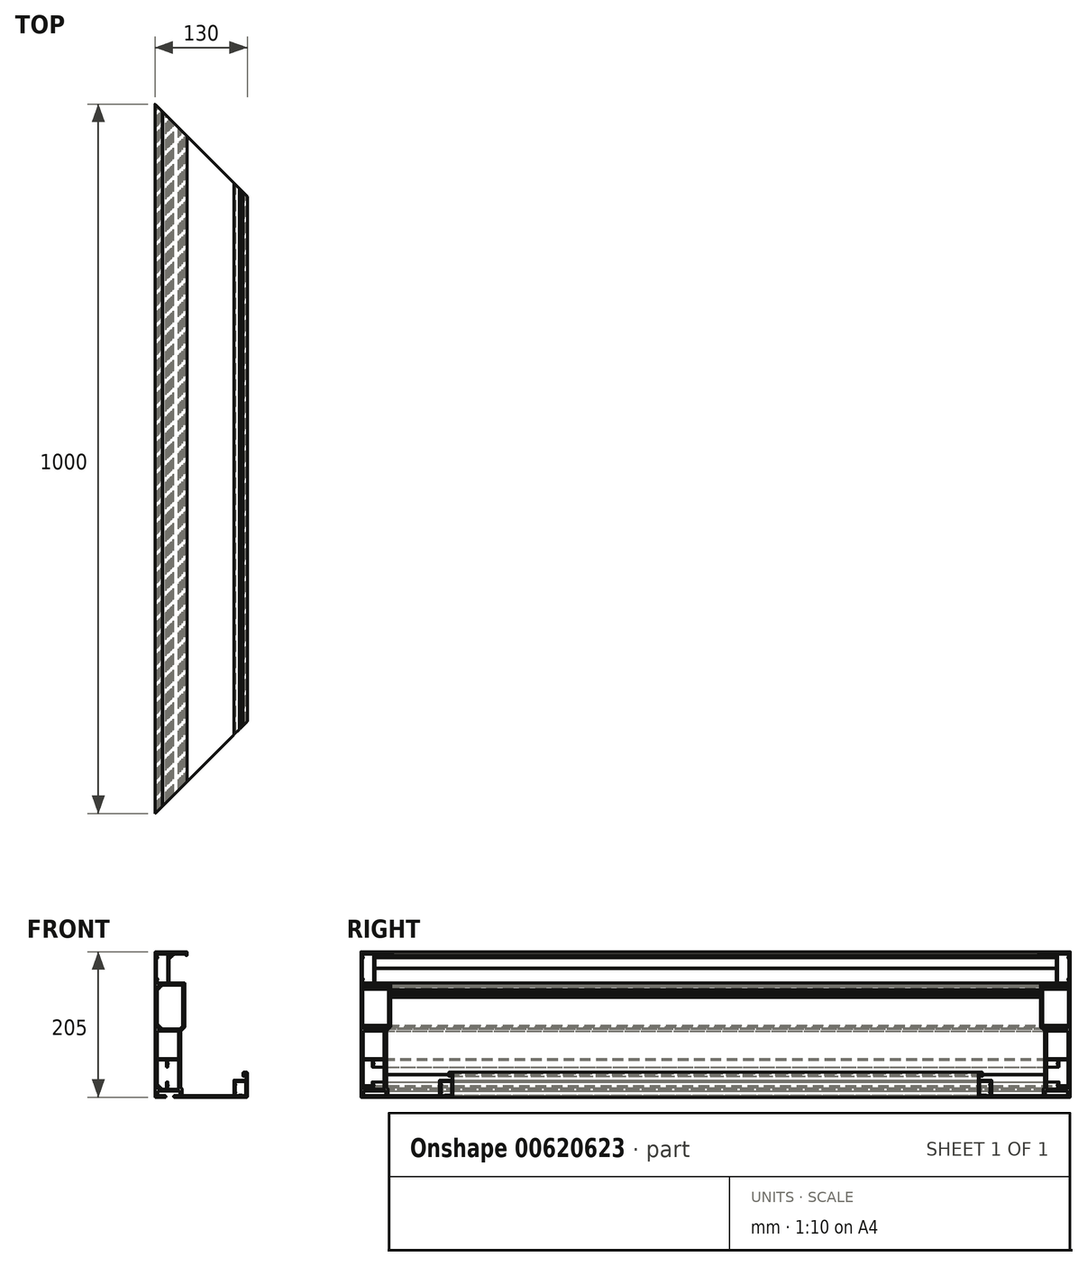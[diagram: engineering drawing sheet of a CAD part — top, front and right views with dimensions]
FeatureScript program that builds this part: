
annotation { "Feature Type Name" : "Feature", "Feature Type Description" : "" }
export const myFeature = defineFeature(function(context is Context, id is Id, definition is map)
    precondition{}
    {
        {
            var Q0;
            Q0=qCreatedBy(makeId("Front.planeOp"),FACE);
            var sketch = newSketch(context, id + "F0", { "sketchPlane" : qUnion([Q0])});
            skArc(sketch, "E0", {"start": v(124.96, 29.38) * mm, "mid": v(124.97, 29.38) * mm, "end": v(124.98, 29.38) * mm});
            skLineSegment(sketch, "E1", {"start": v(10.55, 204.65) * mm, "end": v(10.2, 205) * mm});
            skLineSegment(sketch, "E2", {"start": v(10.2, 205) * mm, "end": v(0.5, 205) * mm});
            skArc(sketch, "E3", {"start": v(0.5, 205) * mm, "mid": v(0.15, 204.85) * mm, "end": v(0, 204.5) * mm});
            skLineSegment(sketch, "E4", {"start": v(0, 204.5) * mm, "end": v(0, 0.5) * mm});
            skArc(sketch, "E5", {"start": v(0, 0.5) * mm, "mid": v(0.15, 0.15) * mm, "end": v(0.5, 0) * mm});
            skLineSegment(sketch, "E6", {"start": v(0.5, 0) * mm, "end": v(14.86, 0) * mm});
            skArc(sketch, "E7", {"start": v(14.86, 0) * mm, "mid": v(15, 0.06) * mm, "end": v(15.06, 0.2) * mm});
            skLineSegment(sketch, "E8", {"start": v(15.06, 0.2) * mm, "end": v(15.06, 1.8) * mm});
            skArc(sketch, "E9", {"start": v(15.06, 1.8) * mm, "mid": v(15, 1.94) * mm, "end": v(14.86, 2) * mm});
            skLineSegment(sketch, "E10", {"start": v(14.86, 2) * mm, "end": v(4.18, 2) * mm});
            skArc(sketch, "E11", {"start": v(4.18, 2) * mm, "mid": v(4.04, 2.06) * mm, "end": v(3.98, 2.2) * mm});
            skLineSegment(sketch, "E12", {"start": v(3.98, 2.2) * mm, "end": v(3.98, 8.3) * mm});
            skArc(sketch, "E13", {"start": v(3.98, 8.3) * mm, "mid": v(4.04, 8.44) * mm, "end": v(4.18, 8.5) * mm});
            skLineSegment(sketch, "E14", {"start": v(4.18, 8.5) * mm, "end": v(25.44, 8.5) * mm});
            skLineSegment(sketch, "E15", {"start": v(25.44, 8.5) * mm, "end": v(25.79, 8.85) * mm});
            skLineSegment(sketch, "E16", {"start": v(25.79, 8.85) * mm, "end": v(26.14, 8.5) * mm});
            skLineSegment(sketch, "E17", {"start": v(26.14, 8.5) * mm, "end": v(34.78, 8.5) * mm});
            skArc(sketch, "E18", {"start": v(34.78, 8.5) * mm, "mid": v(34.93, 8.44) * mm, "end": v(34.98, 8.3) * mm});
            skLineSegment(sketch, "E19", {"start": v(34.98, 8.3) * mm, "end": v(34.98, 2.2) * mm});
            skArc(sketch, "E20", {"start": v(34.98, 2.2) * mm, "mid": v(34.93, 2.06) * mm, "end": v(34.78, 2) * mm});
            skLineSegment(sketch, "E21", {"start": v(34.78, 2) * mm, "end": v(26.58, 2) * mm});
            skArc(sketch, "E22", {"start": v(26.58, 2) * mm, "mid": v(26.44, 1.94) * mm, "end": v(26.38, 1.8) * mm});
            skLineSegment(sketch, "E23", {"start": v(26.38, 1.8) * mm, "end": v(26.38, 0.2) * mm});
            skArc(sketch, "E24", {"start": v(26.38, 0.2) * mm, "mid": v(26.44, 0.06) * mm, "end": v(26.58, 0) * mm});
            skLineSegment(sketch, "E25", {"start": v(26.58, 0) * mm, "end": v(129.5, 0) * mm});
            skArc(sketch, "E26", {"start": v(129.5, 0) * mm, "mid": v(129.85, 0.15) * mm, "end": v(130, 0.5) * mm});
            skLineSegment(sketch, "E27", {"start": v(130, 0.5) * mm, "end": v(130, 34.5) * mm});
            skArc(sketch, "E28", {"start": v(130, 34.5) * mm, "mid": v(129.85, 34.85) * mm, "end": v(129.5, 35) * mm});
            skLineSegment(sketch, "E29", {"start": v(129.5, 35) * mm, "end": v(124.38, 35) * mm});
            skArc(sketch, "E30", {"start": v(124.38, 35) * mm, "mid": v(124.02, 34.85) * mm, "end": v(123.88, 34.5) * mm});
            skLineSegment(sketch, "E31", {"start": v(123.88, 34.5) * mm, "end": v(123.88, 29.88) * mm});
            skArc(sketch, "E32", {"start": v(123.88, 29.88) * mm, "mid": v(124.02, 29.52) * mm, "end": v(124.38, 29.38) * mm});
            skLineSegment(sketch, "E33", {"start": v(124.38, 29.38) * mm, "end": v(125.5, 29.38) * mm});
            skArc(sketch, "E34", {"start": v(125.5, 29.38) * mm, "mid": v(125.51, 29.5) * mm, "end": v(125.58, 29.58) * mm});
            skArc(sketch, "E35", {"start": v(125.58, 29.58) * mm, "mid": v(125.96, 30.25) * mm, "end": v(125.75, 31) * mm});
            skArc(sketch, "E36", {"start": v(125.75, 31) * mm, "mid": v(127, 33.6) * mm, "end": v(128.25, 31) * mm});
            skArc(sketch, "E37", {"start": v(128.25, 31) * mm, "mid": v(128.04, 30.25) * mm, "end": v(128.42, 29.58) * mm});
            skArc(sketch, "E38", {"start": v(128.42, 29.58) * mm, "mid": v(128.48, 29.51) * mm, "end": v(128.5, 29.43) * mm});
            skLineSegment(sketch, "E39", {"start": v(128.5, 29.43) * mm, "end": v(128.5, 24.5) * mm});
            skArc(sketch, "E40", {"start": v(128.5, 24.5) * mm, "mid": v(128.35, 24.15) * mm, "end": v(128, 24) * mm});
            skLineSegment(sketch, "E41", {"start": v(128, 24) * mm, "end": v(119.23, 24) * mm});
            skLineSegment(sketch, "E42", {"start": v(119.23, 24) * mm, "end": v(118.88, 23.65) * mm});
            skLineSegment(sketch, "E43", {"start": v(118.88, 23.65) * mm, "end": v(118.53, 24) * mm});
            skLineSegment(sketch, "E44", {"start": v(118.53, 24) * mm, "end": v(111.5, 24) * mm});
            skArc(sketch, "E45", {"start": v(111.5, 24) * mm, "mid": v(111.15, 23.85) * mm, "end": v(111, 23.5) * mm});
            skLineSegment(sketch, "E46", {"start": v(111, 23.5) * mm, "end": v(111, 2.5) * mm});
            skArc(sketch, "E47", {"start": v(111, 2.5) * mm, "mid": v(110.85, 2.15) * mm, "end": v(110.5, 2) * mm});
            skLineSegment(sketch, "E48", {"start": v(110.5, 2) * mm, "end": v(38.98, 2) * mm});
            skArc(sketch, "E49", {"start": v(38.98, 2) * mm, "mid": v(38.63, 2.15) * mm, "end": v(38.48, 2.5) * mm});
            skLineSegment(sketch, "E50", {"start": v(38.48, 2.5) * mm, "end": v(38.48, 11.3) * mm});
            skArc(sketch, "E51", {"start": v(38.48, 11.3) * mm, "mid": v(38.45, 11.48) * mm, "end": v(38.34, 11.64) * mm});
            skLineSegment(sketch, "E52", {"start": v(38.34, 11.64) * mm, "end": v(36.65, 13.33) * mm});
            skArc(sketch, "E53", {"start": v(36.65, 13.33) * mm, "mid": v(36.54, 13.5) * mm, "end": v(36.5, 13.69) * mm});
            skLineSegment(sketch, "E54", {"start": v(36.5, 13.69) * mm, "end": v(36.5, 31.65) * mm});
            skLineSegment(sketch, "E55", {"start": v(36.5, 31.65) * mm, "end": v(36.15, 32) * mm});
            skLineSegment(sketch, "E56", {"start": v(36.15, 32) * mm, "end": v(36.5, 32.35) * mm});
            skLineSegment(sketch, "E57", {"start": v(36.5, 32.35) * mm, "end": v(36.5, 93.21) * mm});
            skArc(sketch, "E58", {"start": v(36.5, 93.21) * mm, "mid": v(36.54, 93.4) * mm, "end": v(36.65, 93.56) * mm});
            skLineSegment(sketch, "E59", {"start": v(36.65, 93.56) * mm, "end": v(41.86, 98.77) * mm});
            skArc(sketch, "E60", {"start": v(41.86, 98.77) * mm, "mid": v(41.97, 98.93) * mm, "end": v(42, 99.13) * mm});
            skLineSegment(sketch, "E61", {"start": v(42, 99.13) * mm, "end": v(42, 140.65) * mm});
            skLineSegment(sketch, "E62", {"start": v(42, 140.65) * mm, "end": v(41.65, 141) * mm});
            skLineSegment(sketch, "E63", {"start": v(41.65, 141) * mm, "end": v(42, 141.35) * mm});
            skLineSegment(sketch, "E64", {"start": v(42, 141.35) * mm, "end": v(42, 145.65) * mm});
            skLineSegment(sketch, "E65", {"start": v(42, 145.65) * mm, "end": v(41.65, 146) * mm});
            skLineSegment(sketch, "E66", {"start": v(41.65, 146) * mm, "end": v(42, 146.35) * mm});
            skLineSegment(sketch, "E67", {"start": v(42, 146.35) * mm, "end": v(42, 150.65) * mm});
            skLineSegment(sketch, "E68", {"start": v(42, 150.65) * mm, "end": v(41.65, 151) * mm});
            skLineSegment(sketch, "E69", {"start": v(41.65, 151) * mm, "end": v(42, 151.35) * mm});
            skLineSegment(sketch, "E70", {"start": v(42, 151.35) * mm, "end": v(42, 160.5) * mm});
            skArc(sketch, "E71", {"start": v(42, 160.5) * mm, "mid": v(41.86, 160.85) * mm, "end": v(41.5, 161) * mm});
            skLineSegment(sketch, "E72", {"start": v(41.5, 161) * mm, "end": v(20.5, 161) * mm});
            skArc(sketch, "E73", {"start": v(20.5, 161) * mm, "mid": v(20.15, 161.15) * mm, "end": v(20, 161.5) * mm});
            skLineSegment(sketch, "E74", {"start": v(20, 161.5) * mm, "end": v(20, 181.15) * mm});
            skLineSegment(sketch, "E75", {"start": v(20, 181.15) * mm, "end": v(19.65, 181.5) * mm});
            skLineSegment(sketch, "E76", {"start": v(19.65, 181.5) * mm, "end": v(20, 181.85) * mm});
            skLineSegment(sketch, "E77", {"start": v(20, 181.85) * mm, "end": v(20, 195.92) * mm});
            skArc(sketch, "E78", {"start": v(20, 195.92) * mm, "mid": v(20.15, 196.28) * mm, "end": v(20.5, 196.42) * mm});
            skLineSegment(sketch, "E79", {"start": v(20.5, 196.42) * mm, "end": v(21.79, 196.42) * mm});
            skArc(sketch, "E80", {"start": v(21.79, 196.42) * mm, "mid": v(22.77, 197.36) * mm, "end": v(21.88, 198.38) * mm});
            skArc(sketch, "E81", {"start": v(21.88, 198.38) * mm, "mid": v(20.84, 201.15) * mm, "end": v(23.62, 200.14) * mm});
            skArc(sketch, "E82", {"start": v(23.62, 200.14) * mm, "mid": v(24.63, 199.23) * mm, "end": v(25.58, 200.21) * mm});
            skLineSegment(sketch, "E83", {"start": v(25.58, 200.21) * mm, "end": v(25.58, 201.5) * mm});
            skArc(sketch, "E84", {"start": v(25.58, 201.5) * mm, "mid": v(25.72, 201.85) * mm, "end": v(26.08, 202) * mm});
            skLineSegment(sketch, "E85", {"start": v(26.08, 202) * mm, "end": v(43.2, 202) * mm});
            skArc(sketch, "E86", {"start": v(43.2, 202) * mm, "mid": v(43.55, 201.85) * mm, "end": v(43.7, 201.5) * mm});
            skLineSegment(sketch, "E87", {"start": v(43.7, 201.5) * mm, "end": v(43.7, 199.7) * mm});
            skArc(sketch, "E88", {"start": v(43.7, 199.7) * mm, "mid": v(43.76, 199.56) * mm, "end": v(43.9, 199.5) * mm});
            skLineSegment(sketch, "E89", {"start": v(43.9, 199.5) * mm, "end": v(44.8, 199.5) * mm});
            skArc(sketch, "E90", {"start": v(44.8, 199.5) * mm, "mid": v(44.94, 199.56) * mm, "end": v(45, 199.7) * mm});
            skLineSegment(sketch, "E91", {"start": v(45, 199.7) * mm, "end": v(45, 204.5) * mm});
            skArc(sketch, "E92", {"start": v(45, 204.5) * mm, "mid": v(44.85, 204.85) * mm, "end": v(44.5, 205) * mm});
            skLineSegment(sketch, "E93", {"start": v(44.5, 205) * mm, "end": v(10.9, 205) * mm});
            skLineSegment(sketch, "E94", {"start": v(10.9, 205) * mm, "end": v(10.55, 204.65) * mm});
            skLineSegment(sketch, "E95", {"start": v(3.3, 161) * mm, "end": v(17.8, 161) * mm});
            skArc(sketch, "E96", {"start": v(17.8, 161) * mm, "mid": v(17.94, 161.06) * mm, "end": v(18, 161.2) * mm});
            skLineSegment(sketch, "E97", {"start": v(18, 161.2) * mm, "end": v(18, 201.8) * mm});
            skArc(sketch, "E98", {"start": v(18, 201.8) * mm, "mid": v(17.94, 201.94) * mm, "end": v(17.8, 202) * mm});
            skLineSegment(sketch, "E99", {"start": v(17.8, 202) * mm, "end": v(3.3, 202) * mm});
            skArc(sketch, "E100", {"start": v(3.3, 202) * mm, "mid": v(3.16, 201.94) * mm, "end": v(3.1, 201.8) * mm});
            skLineSegment(sketch, "E101", {"start": v(3.1, 201.8) * mm, "end": v(3.1, 197.89) * mm});
            skArc(sketch, "E102", {"start": v(3.1, 197.89) * mm, "mid": v(3.12, 197.81) * mm, "end": v(3.16, 197.75) * mm});
            skLineSegment(sketch, "E103", {"start": v(3.16, 197.75) * mm, "end": v(3.64, 197.26) * mm});
            skArc(sketch, "E104", {"start": v(3.64, 197.26) * mm, "mid": v(3.68, 197.2) * mm, "end": v(3.7, 197.12) * mm});
            skLineSegment(sketch, "E105", {"start": v(3.7, 197.12) * mm, "end": v(3.7, 196.29) * mm});
            skArc(sketch, "E106", {"start": v(3.7, 196.29) * mm, "mid": v(3.68, 196.21) * mm, "end": v(3.64, 196.15) * mm});
            skLineSegment(sketch, "E107", {"start": v(3.64, 196.15) * mm, "end": v(2.15, 194.65) * mm});
            skArc(sketch, "E108", {"start": v(2.15, 194.65) * mm, "mid": v(2.04, 194.49) * mm, "end": v(2, 194.3) * mm});
            skLineSegment(sketch, "E109", {"start": v(2, 194.3) * mm, "end": v(2, 168.7) * mm});
            skArc(sketch, "E110", {"start": v(2, 168.7) * mm, "mid": v(2.04, 168.51) * mm, "end": v(2.15, 168.35) * mm});
            skLineSegment(sketch, "E111", {"start": v(2.15, 168.35) * mm, "end": v(3.64, 166.85) * mm});
            skArc(sketch, "E112", {"start": v(3.64, 166.85) * mm, "mid": v(3.68, 166.79) * mm, "end": v(3.7, 166.71) * mm});
            skLineSegment(sketch, "E113", {"start": v(3.7, 166.71) * mm, "end": v(3.7, 165.88) * mm});
            skArc(sketch, "E114", {"start": v(3.7, 165.88) * mm, "mid": v(3.68, 165.8) * mm, "end": v(3.64, 165.74) * mm});
            skLineSegment(sketch, "E115", {"start": v(3.64, 165.74) * mm, "end": v(3.16, 165.25) * mm});
            skArc(sketch, "E116", {"start": v(3.16, 165.25) * mm, "mid": v(3.12, 165.19) * mm, "end": v(3.1, 165.11) * mm});
            skLineSegment(sketch, "E117", {"start": v(3.1, 165.11) * mm, "end": v(3.1, 161.2) * mm});
            skArc(sketch, "E118", {"start": v(3.1, 161.2) * mm, "mid": v(3.16, 161.06) * mm, "end": v(3.3, 161) * mm});
            skLineSegment(sketch, "E119", {"start": v(8.58, 96.5) * mm, "end": v(8.58, 97.79) * mm});
            skArc(sketch, "E120", {"start": v(8.58, 97.79) * mm, "mid": v(7.63, 98.77) * mm, "end": v(6.62, 97.86) * mm});
            skArc(sketch, "E121", {"start": v(6.62, 97.86) * mm, "mid": v(3.84, 96.85) * mm, "end": v(4.88, 99.62) * mm});
            skArc(sketch, "E122", {"start": v(4.88, 99.62) * mm, "mid": v(5.77, 100.64) * mm, "end": v(4.79, 101.58) * mm});
            skLineSegment(sketch, "E123", {"start": v(4.79, 101.58) * mm, "end": v(3.5, 101.58) * mm});
            skArc(sketch, "E124", {"start": v(3.5, 101.58) * mm, "mid": v(3.15, 101.72) * mm, "end": v(3, 102.08) * mm});
            skLineSegment(sketch, "E125", {"start": v(3, 102.08) * mm, "end": v(3, 151.92) * mm});
            skArc(sketch, "E126", {"start": v(3, 151.92) * mm, "mid": v(3.15, 152.28) * mm, "end": v(3.5, 152.42) * mm});
            skLineSegment(sketch, "E127", {"start": v(3.5, 152.42) * mm, "end": v(4.79, 152.42) * mm});
            skArc(sketch, "E128", {"start": v(4.79, 152.42) * mm, "mid": v(5.77, 153.36) * mm, "end": v(4.88, 154.38) * mm});
            skArc(sketch, "E129", {"start": v(4.88, 154.38) * mm, "mid": v(3.84, 157.15) * mm, "end": v(6.62, 156.14) * mm});
            skArc(sketch, "E130", {"start": v(6.62, 156.14) * mm, "mid": v(7.63, 155.23) * mm, "end": v(8.58, 156.21) * mm});
            skLineSegment(sketch, "E131", {"start": v(8.58, 156.21) * mm, "end": v(8.58, 157.5) * mm});
            skArc(sketch, "E132", {"start": v(8.58, 157.5) * mm, "mid": v(8.72, 157.85) * mm, "end": v(9.08, 158) * mm});
            skLineSegment(sketch, "E133", {"start": v(9.08, 158) * mm, "end": v(38.5, 158) * mm});
            skArc(sketch, "E134", {"start": v(38.5, 158) * mm, "mid": v(38.85, 157.85) * mm, "end": v(39, 157.5) * mm});
            skLineSegment(sketch, "E135", {"start": v(39, 157.5) * mm, "end": v(39, 100.43) * mm});
            skArc(sketch, "E136", {"start": v(39, 100.43) * mm, "mid": v(38.96, 100.24) * mm, "end": v(38.85, 100.07) * mm});
            skLineSegment(sketch, "E137", {"start": v(38.85, 100.07) * mm, "end": v(34.93, 96.15) * mm});
            skArc(sketch, "E138", {"start": v(34.93, 96.15) * mm, "mid": v(34.76, 96.04) * mm, "end": v(34.57, 96) * mm});
            skLineSegment(sketch, "E139", {"start": v(34.57, 96) * mm, "end": v(9.08, 96) * mm});
            skArc(sketch, "E140", {"start": v(9.08, 96) * mm, "mid": v(8.72, 96.15) * mm, "end": v(8.58, 96.5) * mm});
            skLineSegment(sketch, "E141", {"start": v(3.5, 54.67) * mm, "end": v(3.5, 92.8) * mm});
            skArc(sketch, "E142", {"start": v(3.5, 92.8) * mm, "mid": v(3.56, 92.94) * mm, "end": v(3.7, 93) * mm});
            skLineSegment(sketch, "E143", {"start": v(3.7, 93) * mm, "end": v(32.74, 93) * mm});
            skArc(sketch, "E144", {"start": v(32.74, 93) * mm, "mid": v(32.88, 92.94) * mm, "end": v(32.94, 92.8) * mm});
            skLineSegment(sketch, "E145", {"start": v(32.94, 92.8) * mm, "end": v(32.94, 54.67) * mm});
            skArc(sketch, "E146", {"start": v(32.94, 54.67) * mm, "mid": v(32.88, 54.53) * mm, "end": v(32.74, 54.47) * mm});
            skLineSegment(sketch, "E147", {"start": v(32.74, 54.47) * mm, "end": v(3.7, 54.47) * mm});
            skArc(sketch, "E148", {"start": v(3.7, 54.47) * mm, "mid": v(3.56, 54.53) * mm, "end": v(3.5, 54.67) * mm});
            skLineSegment(sketch, "E149", {"start": v(32.94, 52) * mm, "end": v(32.94, 12) * mm});
            skLineSegment(sketch, "E150", {"start": v(18.04, 21.3) * mm, "end": v(18.04, 17.97) * mm});
            skArc(sketch, "E151", {"start": v(18.04, 17.97) * mm, "mid": v(18.05, 17.9) * mm, "end": v(18.1, 17.83) * mm});
            skLineSegment(sketch, "E152", {"start": v(18.1, 17.83) * mm, "end": v(18.58, 17.35) * mm});
            skArc(sketch, "E153", {"start": v(18.58, 17.35) * mm, "mid": v(18.62, 17.29) * mm, "end": v(18.64, 17.2) * mm});
            skLineSegment(sketch, "E154", {"start": v(18.64, 17.2) * mm, "end": v(18.64, 16.37) * mm});
            skArc(sketch, "E155", {"start": v(18.64, 16.37) * mm, "mid": v(18.62, 16.3) * mm, "end": v(18.58, 16.23) * mm});
            skLineSegment(sketch, "E156", {"start": v(18.58, 16.23) * mm, "end": v(18.1, 15.75) * mm});
            skArc(sketch, "E157", {"start": v(18.1, 15.75) * mm, "mid": v(18.05, 15.69) * mm, "end": v(18.04, 15.6) * mm});
            skLineSegment(sketch, "E158", {"start": v(18.04, 15.6) * mm, "end": v(18.04, 11.7) * mm});
            skArc(sketch, "E159", {"start": v(18.04, 11.7) * mm, "mid": v(18.1, 11.56) * mm, "end": v(18.24, 11.5) * mm});
            skLineSegment(sketch, "E160", {"start": v(18.24, 11.5) * mm, "end": v(32.74, 11.5) * mm});
            skArc(sketch, "E161", {"start": v(32.74, 11.5) * mm, "mid": v(32.88, 11.56) * mm, "end": v(32.94, 11.7) * mm});
            skLineSegment(sketch, "E162", {"start": v(32.94, 11.7) * mm, "end": v(32.94, 52.3) * mm});
            skArc(sketch, "E163", {"start": v(32.94, 52.3) * mm, "mid": v(32.88, 52.44) * mm, "end": v(32.74, 52.5) * mm});
            skLineSegment(sketch, "E164", {"start": v(32.74, 52.5) * mm, "end": v(18.24, 52.5) * mm});
            skArc(sketch, "E165", {"start": v(18.24, 52.5) * mm, "mid": v(18.1, 52.44) * mm, "end": v(18.04, 52.3) * mm});
            skLineSegment(sketch, "E166", {"start": v(18.04, 52.3) * mm, "end": v(18.04, 48.39) * mm});
            skArc(sketch, "E167", {"start": v(18.04, 48.39) * mm, "mid": v(18.05, 48.3) * mm, "end": v(18.1, 48.24) * mm});
            skLineSegment(sketch, "E168", {"start": v(18.1, 48.24) * mm, "end": v(18.58, 47.76) * mm});
            skArc(sketch, "E169", {"start": v(18.58, 47.76) * mm, "mid": v(18.62, 47.7) * mm, "end": v(18.64, 47.62) * mm});
            skLineSegment(sketch, "E170", {"start": v(18.64, 47.62) * mm, "end": v(18.64, 46.79) * mm});
            skArc(sketch, "E171", {"start": v(18.64, 46.79) * mm, "mid": v(18.62, 46.7) * mm, "end": v(18.58, 46.64) * mm});
            skLineSegment(sketch, "E172", {"start": v(18.58, 46.64) * mm, "end": v(18.1, 46.16) * mm});
            skArc(sketch, "E173", {"start": v(18.1, 46.16) * mm, "mid": v(18.05, 46.1) * mm, "end": v(18.04, 46.02) * mm});
            skLineSegment(sketch, "E174", {"start": v(18.04, 46.02) * mm, "end": v(18.04, 42.7) * mm});
            skArc(sketch, "E175", {"start": v(18.04, 42.7) * mm, "mid": v(17.98, 42.56) * mm, "end": v(17.84, 42.5) * mm});
            skLineSegment(sketch, "E176", {"start": v(17.84, 42.5) * mm, "end": v(16.25, 42.5) * mm});
            skArc(sketch, "E177", {"start": v(16.25, 42.5) * mm, "mid": v(16.11, 42.56) * mm, "end": v(16.05, 42.7) * mm});
            skLineSegment(sketch, "E178", {"start": v(16.05, 42.7) * mm, "end": v(16.05, 52.3) * mm});
            skArc(sketch, "E179", {"start": v(16.05, 52.3) * mm, "mid": v(16, 52.44) * mm, "end": v(15.85, 52.5) * mm});
            skLineSegment(sketch, "E180", {"start": v(15.85, 52.5) * mm, "end": v(3.7, 52.5) * mm});
            skArc(sketch, "E181", {"start": v(3.7, 52.5) * mm, "mid": v(3.56, 52.44) * mm, "end": v(3.5, 52.3) * mm});
            skLineSegment(sketch, "E182", {"start": v(3.5, 52.3) * mm, "end": v(3.5, 17.58) * mm});
            skArc(sketch, "E183", {"start": v(3.5, 17.58) * mm, "mid": v(3.8, 16.87) * mm, "end": v(4.5, 16.58) * mm});
            skLineSegment(sketch, "E184", {"start": v(4.5, 16.58) * mm, "end": v(4.79, 16.58) * mm});
            skArc(sketch, "E185", {"start": v(4.79, 16.58) * mm, "mid": v(5.77, 15.64) * mm, "end": v(4.88, 14.62) * mm});
            skArc(sketch, "E186", {"start": v(4.88, 14.62) * mm, "mid": v(3.84, 11.85) * mm, "end": v(6.62, 12.86) * mm});
            skArc(sketch, "E187", {"start": v(6.62, 12.86) * mm, "mid": v(7.63, 13.77) * mm, "end": v(8.58, 12.79) * mm});
            skLineSegment(sketch, "E188", {"start": v(8.58, 12.79) * mm, "end": v(8.58, 12.5) * mm});
            skArc(sketch, "E189", {"start": v(8.58, 12.5) * mm, "mid": v(8.87, 11.8) * mm, "end": v(9.58, 11.5) * mm});
            skLineSegment(sketch, "E190", {"start": v(9.58, 11.5) * mm, "end": v(15.55, 11.5) * mm});
            skArc(sketch, "E191", {"start": v(15.55, 11.5) * mm, "mid": v(15.9, 11.64) * mm, "end": v(16.05, 12) * mm});
            skLineSegment(sketch, "E192", {"start": v(16.05, 12) * mm, "end": v(16.05, 21.3) * mm});
            skArc(sketch, "E193", {"start": v(16.05, 21.3) * mm, "mid": v(16.11, 21.44) * mm, "end": v(16.25, 21.5) * mm});
            skLineSegment(sketch, "E194", {"start": v(16.25, 21.5) * mm, "end": v(17.84, 21.5) * mm});
            skArc(sketch, "E195", {"start": v(17.84, 21.5) * mm, "mid": v(17.98, 21.44) * mm, "end": v(18.04, 21.3) * mm});
            skLineSegment(sketch, "E196", {"start": v(122.56, 2.94) * mm, "end": v(123.44, 2.06) * mm});
            skArc(sketch, "E197", {"start": v(123.44, 2.06) * mm, "mid": v(123.5, 2.02) * mm, "end": v(123.58, 2) * mm});
            skLineSegment(sketch, "E198", {"start": v(123.58, 2) * mm, "end": v(127.8, 2) * mm});
            skArc(sketch, "E199", {"start": v(127.8, 2) * mm, "mid": v(127.94, 2.06) * mm, "end": v(128, 2.2) * mm});
            skLineSegment(sketch, "E200", {"start": v(128, 2.2) * mm, "end": v(128, 21.8) * mm});
            skArc(sketch, "E201", {"start": v(128, 21.8) * mm, "mid": v(127.94, 21.94) * mm, "end": v(127.8, 22) * mm});
            skLineSegment(sketch, "E202", {"start": v(127.8, 22) * mm, "end": v(113.2, 22) * mm});
            skArc(sketch, "E203", {"start": v(113.2, 22) * mm, "mid": v(113.06, 21.94) * mm, "end": v(113, 21.8) * mm});
            skLineSegment(sketch, "E204", {"start": v(113, 21.8) * mm, "end": v(113, 18.78) * mm});
            skArc(sketch, "E205", {"start": v(113, 18.78) * mm, "mid": v(113.02, 18.7) * mm, "end": v(113.06, 18.64) * mm});
            skLineSegment(sketch, "E206", {"start": v(113.06, 18.64) * mm, "end": v(113.64, 18.06) * mm});
            skArc(sketch, "E207", {"start": v(113.64, 18.06) * mm, "mid": v(113.68, 18) * mm, "end": v(113.7, 17.92) * mm});
            skLineSegment(sketch, "E208", {"start": v(113.7, 17.92) * mm, "end": v(113.7, 17.08) * mm});
            skArc(sketch, "E209", {"start": v(113.7, 17.08) * mm, "mid": v(113.68, 17) * mm, "end": v(113.64, 16.94) * mm});
            skLineSegment(sketch, "E210", {"start": v(113.64, 16.94) * mm, "end": v(113.06, 16.36) * mm});
            skArc(sketch, "E211", {"start": v(113.06, 16.36) * mm, "mid": v(113.02, 16.3) * mm, "end": v(113, 16.22) * mm});
            skLineSegment(sketch, "E212", {"start": v(113, 16.22) * mm, "end": v(113, 7.78) * mm});
            skArc(sketch, "E213", {"start": v(113, 7.78) * mm, "mid": v(113.02, 7.7) * mm, "end": v(113.06, 7.64) * mm});
            skLineSegment(sketch, "E214", {"start": v(113.06, 7.64) * mm, "end": v(113.64, 7.06) * mm});
            skArc(sketch, "E215", {"start": v(113.64, 7.06) * mm, "mid": v(113.68, 7) * mm, "end": v(113.7, 6.92) * mm});
            skLineSegment(sketch, "E216", {"start": v(113.7, 6.92) * mm, "end": v(113.7, 6.08) * mm});
            skArc(sketch, "E217", {"start": v(113.7, 6.08) * mm, "mid": v(113.68, 6) * mm, "end": v(113.64, 5.94) * mm});
            skLineSegment(sketch, "E218", {"start": v(113.64, 5.94) * mm, "end": v(113.06, 5.36) * mm});
            skArc(sketch, "E219", {"start": v(113.06, 5.36) * mm, "mid": v(113.02, 5.3) * mm, "end": v(113, 5.22) * mm});
            skLineSegment(sketch, "E220", {"start": v(113, 5.22) * mm, "end": v(113, 2.2) * mm});
            skArc(sketch, "E221", {"start": v(113, 2.2) * mm, "mid": v(113.06, 2.06) * mm, "end": v(113.2, 2) * mm});
            skLineSegment(sketch, "E222", {"start": v(113.2, 2) * mm, "end": v(117.42, 2) * mm});
            skArc(sketch, "E223", {"start": v(117.42, 2) * mm, "mid": v(117.5, 2.02) * mm, "end": v(117.56, 2.06) * mm});
            skLineSegment(sketch, "E224", {"start": v(117.56, 2.06) * mm, "end": v(118.44, 2.94) * mm});
            skArc(sketch, "E225", {"start": v(118.44, 2.94) * mm, "mid": v(118.5, 2.98) * mm, "end": v(118.58, 3) * mm});
            skLineSegment(sketch, "E226", {"start": v(118.58, 3) * mm, "end": v(122.42, 3) * mm});
            skArc(sketch, "E227", {"start": v(122.42, 3) * mm, "mid": v(122.5, 2.98) * mm, "end": v(122.56, 2.94) * mm});
            skLineSegment(sketch, "E228", {"start": v(0, 0.5) * mm, "end": v(0, 0) * mm, "construction": true});
            skLineSegment(sketch, "E229", {"start": v(0.5, 0) * mm, "end": v(0, 0) * mm, "construction": true});
            skSolve(sketch);
        }
        {
            var Q0;
            Q0 = qSketchRegion(id + "F0", true);
            extrude(context, id + "F1", {"entities" : qUnion([Q0]), "endBound" : BoundingType.SYMMETRIC, "depth" : 1000 * mm, "offsetDistance" : 25 * mm});
        }
        {
            var Q0;
            Q0=makeQuery(id+"F1.opExtrude","SWEPT_FACE",FACE,{"disambiguationData":[OSD([sQuery(id+"F0.wireOp",EDGE,"E25")])]});
            var sketch = newSketch(context, id + "F2", { "sketchPlane" : qUnion([Q0])});
            skLineSegment(sketch, "E230", {"start": v(0, 500) * mm, "end": v(130, 370) * mm});
            skLineSegment(sketch, "E231", {"start": v(130, 370) * mm, "end": v(130, 500) * mm});
            skLineSegment(sketch, "E232", {"start": v(130, 500) * mm, "end": v(0, 500) * mm});
            skLineSegment(sketch, "E233", {"start": v(130, 0) * mm, "end": v(-122.96, 0) * mm, "construction": true});
            skLineSegment(sketch, "E234.MirrorCS", {"start": v(130, -500) * mm, "end": v(0, -500) * mm});
            skLineSegment(sketch, "E235.MirrorCS", {"start": v(130, -370) * mm, "end": v(130, -500) * mm});
            skLineSegment(sketch, "E236.MirrorCS", {"start": v(0, -500) * mm, "end": v(130, -370) * mm});
            skSolve(sketch);
        }
        {
            var Q0;
            Q0 = qSketchRegion(id + "F2", true);
            extrude(context, id + "F3", {"entities" : qUnion([Q0]), "operationType" : NewBodyOperationType.REMOVE, "endBound" : BoundingType.THROUGH_ALL, "oppositeDirection" : true, "depth" : 25 * mm, "offsetDistance" : 25 * mm});
        }
    });
